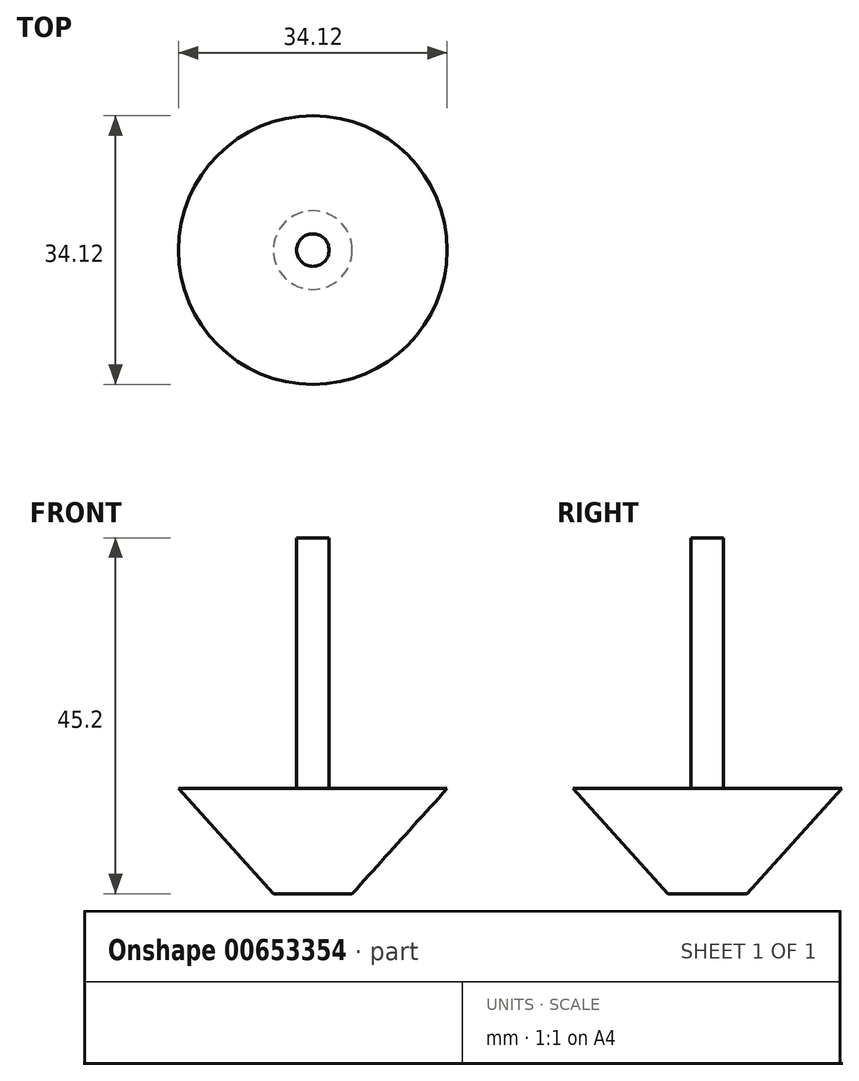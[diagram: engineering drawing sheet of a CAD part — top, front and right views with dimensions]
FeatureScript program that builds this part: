
annotation { "Feature Type Name" : "Feature", "Feature Type Description" : "" }
export const myFeature = defineFeature(function(context is Context, id is Id, definition is map)
    precondition{}
    {
        {
            var Q0;
            Q0=qCreatedBy(makeId("Front.planeOp"),FACE);
            var sketch = newSketch(context, id + "F0", { "sketchPlane" : qUnion([Q0])});
            skLineSegment(sketch, "E0", {"start": v(-17.06, -7.7) * mm, "end": v(-2.06, -7.7) * mm});
            skLineSegment(sketch, "E1", {"start": v(-2.06, 24.15) * mm, "end": v(-2.06, -7.7) * mm});
            skLineSegment(sketch, "E2", {"start": v(-2.06, 24.15) * mm, "end": v(0, 24.1) * mm});
            skLineSegment(sketch, "E3", {"start": v(-17.06, -7.7) * mm, "end": v(-5, -21.05) * mm});
            skLineSegment(sketch, "E4", {"start": v(0, -21.05) * mm, "end": v(-5, -21.05) * mm});
            skLineSegment(sketch, "E5", {"start": v(0, 24.1) * mm, "end": v(0, -21.05) * mm});
            skSolve(sketch);
        }
        {
            var Q0;
            Q0 = qSketchRegion(id + "F0", true);
            var Q1;
            Q1=sQuery(id+"F0.wireOp",EDGE,"E5");
            revolve(context, id + "F1", {"entities" : qUnion([Q0]), "axis" : qUnion([Q1]), "revolveType" : RevolveType.FULL});
        }
    });
